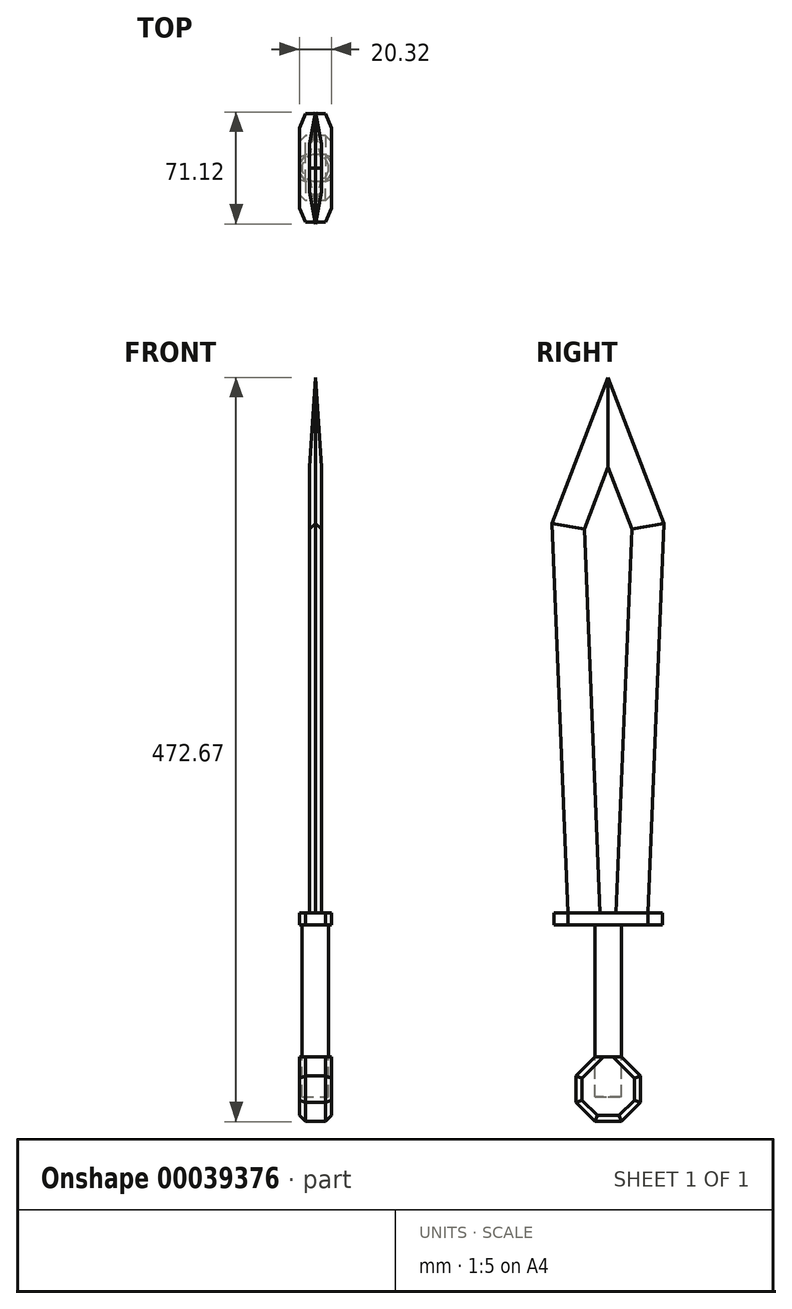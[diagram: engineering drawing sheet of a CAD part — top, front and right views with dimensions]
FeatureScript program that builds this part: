
annotation { "Feature Type Name" : "Feature", "Feature Type Description" : "" }
export const myFeature = defineFeature(function(context is Context, id is Id, definition is map)
    precondition{}
    {
        {
            var Q0;
            Q0=qCreatedBy(makeId("Right.planeOp"),FACE);
            var sketch = newSketch(context, id + "F0", { "sketchPlane" : qUnion([Q0])});
            skLineSegment(sketch, "E0", {"start": v(0, 0) * mm, "end": v(0, 82.4) * mm});
            skLineSegment(sketch, "E1", {"start": v(0, 82.4) * mm, "end": v(0, 0) * mm});
            skLineSegment(sketch, "E2", {"start": v(0, 0) * mm, "end": v(-25.4, 0) * mm});
            skLineSegment(sketch, "E3.MirrorCS", {"start": v(0, 0) * mm, "end": v(25.4, 0) * mm});
            skLineSegment(sketch, "E4", {"start": v(0, 82.4) * mm, "end": v(0, 247.17) * mm});
            skLineSegment(sketch, "E5", {"start": v(0, 247.17) * mm, "end": v(-35.56, 247.17) * mm});
            skLineSegment(sketch, "E6", {"start": v(-35.56, 247.17) * mm, "end": v(35.56, 247.17) * mm});
            skLineSegment(sketch, "E7", {"start": v(-35.56, 247.17) * mm, "end": v(-25.4, 0) * mm});
            skLineSegment(sketch, "E8", {"start": v(35.56, 247.17) * mm, "end": v(25.4, 0) * mm});
            skLineSegment(sketch, "E9", {"start": v(0, 247.17) * mm, "end": v(0, 340.03) * mm});
            skLineSegment(sketch, "E10", {"start": v(0, 340.03) * mm, "end": v(-35.56, 247.17) * mm});
            skLineSegment(sketch, "E11", {"start": v(0, 340.03) * mm, "end": v(35.56, 247.17) * mm});
            skSolve(sketch);
        }
        {
            var Q0;
            Q0 = qSketchRegion(id + "F0", true);
            extrude(context, id + "F1", {"entities" : qUnion([Q0]), "endBound" : BoundingType.SYMMETRIC, "depth" : 7.62 * mm});
        }
        {
            var Q0;
            Q0=makeQuery(id+"F1.opExtrude","CAP_EDGE",EDGE,{"disambiguationData":[OSD([sQuery(id+"F0.wireOp",EDGE,"E7")])],"isStart":false});
            var Q1;
            Q1=makeQuery(id+"F1.opExtrude","CAP_EDGE",EDGE,{"disambiguationData":[OSD([sQuery(id+"F0.wireOp",EDGE,"E10")])],"isStart":false});
            var Q2;
            Q2=makeQuery(id+"F1.opExtrude","CAP_EDGE",EDGE,{"disambiguationData":[OSD([sQuery(id+"F0.wireOp",EDGE,"E11")])],"isStart":false});
            var Q3;
            Q3=makeQuery(id+"F1.opExtrude","CAP_EDGE",EDGE,{"disambiguationData":[OSD([sQuery(id+"F0.wireOp",EDGE,"E8")])],"isStart":false});
            chamfer(context, id + "F2", {"entities" : qUnion([Q0, Q1, Q2, Q3]), "chamferType" : ChamferType.TWO_OFFSETS, "width1" : 20.32 * mm, "oppositeDirection" : false, "width2" : 3.8 * mm, "tangentPropagation" : true});
        }
        {
            var Q0;
            Q0=makeQuery(id+"F1.opExtrude","CAP_EDGE",EDGE,{"disambiguationData":[OSD([sQuery(id+"F0.wireOp",EDGE,"E7")])],"isStart":true});
            var Q1;
            Q1=makeQuery(id+"F1.opExtrude","CAP_EDGE",EDGE,{"disambiguationData":[OSD([sQuery(id+"F0.wireOp",EDGE,"E10")])],"isStart":true});
            var Q2;
            Q2=makeQuery(id+"F1.opExtrude","CAP_EDGE",EDGE,{"disambiguationData":[OSD([sQuery(id+"F0.wireOp",EDGE,"E8")])],"isStart":true});
            var Q3;
            Q3=makeQuery(id+"F1.opExtrude","CAP_EDGE",EDGE,{"disambiguationData":[OSD([sQuery(id+"F0.wireOp",EDGE,"E11")])],"isStart":true});
            chamfer(context, id + "F3", {"entities" : qUnion([Q0, Q1, Q2, Q3]), "chamferType" : ChamferType.TWO_OFFSETS, "width1" : 3.8 * mm, "oppositeDirection" : false, "width2" : 20.32 * mm, "tangentPropagation" : true});
        }
        {
            var Q0;
            Q0=makeQuery(id+"F1.opExtrude","SWEPT_FACE",FACE,{"disambiguationData":[OSD([sQuery(id+"F0.wireOp",EDGE,"E2"),sQuery(id+"F0.wireOp",EDGE,"E3.MirrorCS")])]});
            var sketch = newSketch(context, id + "F4", { "sketchPlane" : qUnion([Q0])});
            skLineSegment(sketch, "E12.0", {"start": v(-6.35, 34.38) * mm, "end": v(6.35, 34.38) * mm});
            skLineSegment(sketch, "E12.1", {"start": v(6.35, 34.38) * mm, "end": v(10.16, 25.4) * mm});
            skLineSegment(sketch, "E12.7", {"start": v(-10.16, 25.4) * mm, "end": v(-6.35, 34.38) * mm});
            skPoint(sketch, "E12.0.midPoint", {"position": v(0, 34.38) * mm});
            skPoint(sketch, "E12.cCircle.center.orphan", {"position": v(0, 0) * mm});
            skLineSegment(sketch, "E13", {"start": v(-10.16, 25.4) * mm, "end": v(-10.16, -25.4) * mm});
            skLineSegment(sketch, "E14", {"start": v(10.16, 25.4) * mm, "end": v(10.16, -25.4) * mm});
            skLineSegment(sketch, "E15", {"start": v(0, 0) * mm, "end": v(-10.16, 0) * mm});
            skLineSegment(sketch, "E16", {"start": v(-10.16, 0) * mm, "end": v(10.16, 0) * mm});
            skLineSegment(sketch, "E17.MirrorCS", {"start": v(-6.35, -34.38) * mm, "end": v(6.35, -34.38) * mm});
            skLineSegment(sketch, "E18.MirrorCS", {"start": v(6.35, -34.38) * mm, "end": v(10.16, -25.4) * mm});
            skLineSegment(sketch, "E19.MirrorCS", {"start": v(-10.16, -25.4) * mm, "end": v(-6.35, -34.38) * mm});
            skSolve(sketch);
        }
        {
            var Q0;
            Q0 = qSketchRegion(id + "F4", true);
            extrude(context, id + "F5", {"entities" : qUnion([Q0]), "depth" : 7.62 * mm});
        }
        {
            var Q0;
            Q0=makeQuery(id+"F5.opExtrude","CAP_FACE",FACE,{"disambiguationData":[OSD([sQuery(id+"F4.wireOp",EDGE,"E12.0"),sQuery(id+"F4.wireOp",EDGE,"E12.1"),sQuery(id+"F4.wireOp",EDGE,"E12.7"),sQuery(id+"F4.wireOp",EDGE,"E13"),sQuery(id+"F4.wireOp",EDGE,"E14"),sQuery(id+"F4.wireOp",EDGE,"E17.MirrorCS"),sQuery(id+"F4.wireOp",EDGE,"E18.MirrorCS"),sQuery(id+"F4.wireOp",EDGE,"E19.MirrorCS")])],"isStart":false});
            var sketch = newSketch(context, id + "F6", { "sketchPlane" : qUnion([Q0])});
            skCircle(sketch, "E20", {"center": v(0, 0) * mm, "radius": 8.53 * mm});
            skSolve(sketch);
        }
        {
            var Q0;
            Q0 = qSketchRegion(id + "F6", true);
            extrude(context, id + "F7", {"entities" : qUnion([Q0]), "depth" : 83.82 * mm});
        }
        {
            var Q0;
            Q0=qCreatedBy(makeId("Right.planeOp"),FACE);
            var sketch = newSketch(context, id + "F8", { "sketchPlane" : qUnion([Q0])});
            skLineSegment(sketch, "E21.0", {"start": v(8.53, -91.44) * mm, "end": v(-8.53, -91.44) * mm});
            skLineSegment(sketch, "E22", {"start": v(0, -91.44) * mm, "end": v(0, -104.14) * mm});
            skPoint(sketch, "E22.endSnap0", {"position": v(0, -91.44) * mm});
            skCircle(sketch, "E23.cCircle", {"center": v(0, -112.04) * mm, "radius": 22.3 * mm, "construction": true});
            skLineSegment(sketch, "E23.0", {"start": v(-8.53, -91.44) * mm, "end": v(8.53, -91.44) * mm});
            skLineSegment(sketch, "E23.1", {"start": v(8.53, -91.44) * mm, "end": v(20.6, -103.5) * mm});
            skLineSegment(sketch, "E23.2", {"start": v(20.6, -103.5) * mm, "end": v(20.6, -120.57) * mm});
            skLineSegment(sketch, "E23.3", {"start": v(20.6, -120.57) * mm, "end": v(8.53, -132.64) * mm});
            skLineSegment(sketch, "E23.4", {"start": v(8.53, -132.64) * mm, "end": v(-8.53, -132.64) * mm});
            skLineSegment(sketch, "E23.5", {"start": v(-8.53, -132.64) * mm, "end": v(-20.6, -120.57) * mm});
            skLineSegment(sketch, "E23.6", {"start": v(-20.6, -120.57) * mm, "end": v(-20.6, -103.5) * mm});
            skLineSegment(sketch, "E23.7", {"start": v(-20.6, -103.5) * mm, "end": v(-8.53, -91.44) * mm});
            skSolve(sketch);
        }
        {
            var Q0;
            Q0=makeQuery(id+"F7.opExtrude","CAP_FACE",FACE,{"disambiguationData":[OSD([sQuery(id+"F6.wireOp",EDGE,"E20")])],"isStart":false});
            var sketch = newSketch(context, id + "F9", { "sketchPlane" : qUnion([Q0])});
            skCircle(sketch, "E24.0", {"center": v(0, 0) * mm, "radius": 8.53 * mm});
            skSolve(sketch);
        }
        {
            var Q0;
            Q0 = qSketchRegion(id + "F9", true);
            extrude(context, id + "F10", {"entities" : qUnion([Q0]), "operationType" : NewBodyOperationType.ADD, "depth" : 25.4 * mm});
        }
        {
            var Q0;
            Q0 = qSketchRegion(id + "F8", true);
            extrude(context, id + "F11", {"entities" : qUnion([Q0]), "endBound" : BoundingType.SYMMETRIC, "depth" : 20.32 * mm});
        }
        {
            var Q0;
            Q0=makeQuery(id+"F11.opExtrude","CAP_EDGE",EDGE,{"disambiguationData":[OSD([sQuery(id+"F8.wireOp",EDGE,"E23.2")])],"isStart":false});
            var Q1;
            Q1=makeQuery(id+"F11.opExtrude","CAP_EDGE",EDGE,{"disambiguationData":[OSD([sQuery(id+"F8.wireOp",EDGE,"E23.1")])],"isStart":false});
            var Q2;
            Q2=makeQuery(id+"F11.opExtrude","CAP_EDGE",EDGE,{"disambiguationData":[OSD([sQuery(id+"F8.wireOp",EDGE,"E23.0")])],"isStart":false});
            var Q3;
            Q3=makeQuery(id+"F11.opExtrude","CAP_EDGE",EDGE,{"disambiguationData":[OSD([sQuery(id+"F8.wireOp",EDGE,"E23.3")])],"isStart":false});
            var Q4;
            Q4=makeQuery(id+"F11.opExtrude","CAP_EDGE",EDGE,{"disambiguationData":[OSD([sQuery(id+"F8.wireOp",EDGE,"E23.4")])],"isStart":false});
            var Q5;
            Q5=makeQuery(id+"F11.opExtrude","CAP_EDGE",EDGE,{"disambiguationData":[OSD([sQuery(id+"F8.wireOp",EDGE,"E23.5")])],"isStart":false});
            var Q6;
            Q6=makeQuery(id+"F11.opExtrude","CAP_EDGE",EDGE,{"disambiguationData":[OSD([sQuery(id+"F8.wireOp",EDGE,"E23.7")])],"isStart":false});
            var Q7;
            Q7=makeQuery(id+"F11.opExtrude","CAP_EDGE",EDGE,{"disambiguationData":[OSD([sQuery(id+"F8.wireOp",EDGE,"E23.6")])],"isStart":false});
            var Q8;
            Q8=makeQuery(id+"F11.opExtrude","CAP_EDGE",EDGE,{"disambiguationData":[OSD([sQuery(id+"F8.wireOp",EDGE,"E23.6")])],"isStart":true});
            var Q9;
            Q9=makeQuery(id+"F11.opExtrude","CAP_EDGE",EDGE,{"disambiguationData":[OSD([sQuery(id+"F8.wireOp",EDGE,"E23.7")])],"isStart":true});
            var Q10;
            Q10=makeQuery(id+"F11.opExtrude","CAP_EDGE",EDGE,{"disambiguationData":[OSD([sQuery(id+"F8.wireOp",EDGE,"E23.5")])],"isStart":true});
            var Q11;
            Q11=makeQuery(id+"F11.opExtrude","CAP_EDGE",EDGE,{"disambiguationData":[OSD([sQuery(id+"F8.wireOp",EDGE,"E23.4")])],"isStart":true});
            var Q12;
            Q12=makeQuery(id+"F11.opExtrude","CAP_EDGE",EDGE,{"disambiguationData":[OSD([sQuery(id+"F8.wireOp",EDGE,"E23.0")])],"isStart":true});
            var Q13;
            Q13=makeQuery(id+"F11.opExtrude","CAP_EDGE",EDGE,{"disambiguationData":[OSD([sQuery(id+"F8.wireOp",EDGE,"E23.1")])],"isStart":true});
            var Q14;
            Q14=makeQuery(id+"F11.opExtrude","CAP_EDGE",EDGE,{"disambiguationData":[OSD([sQuery(id+"F8.wireOp",EDGE,"E23.2")])],"isStart":true});
            var Q15;
            Q15=makeQuery(id+"F11.opExtrude","CAP_EDGE",EDGE,{"disambiguationData":[OSD([sQuery(id+"F8.wireOp",EDGE,"E23.3")])],"isStart":true});
            chamfer(context, id + "F12", {"entities" : qUnion([Q0, Q1, Q2, Q3, Q4, Q5, Q6, Q7, Q8, Q9, Q10, Q11, Q12, Q13, Q14, Q15]), "width" : 3.8 * mm, "tangentPropagation" : true});
        }
    });
